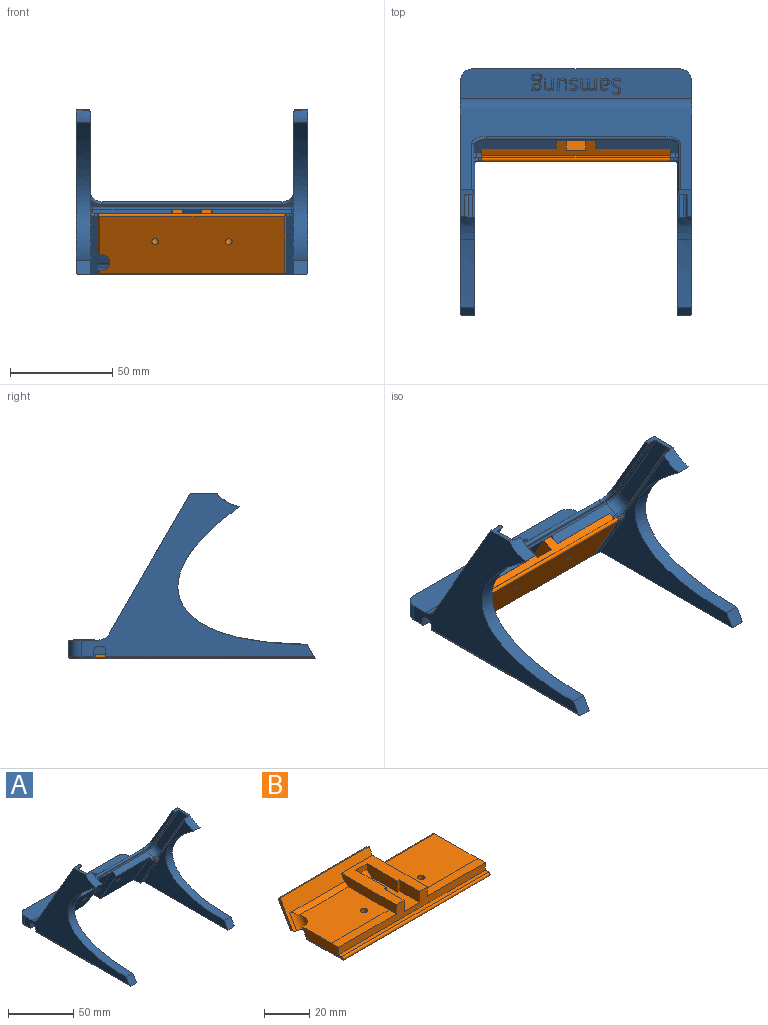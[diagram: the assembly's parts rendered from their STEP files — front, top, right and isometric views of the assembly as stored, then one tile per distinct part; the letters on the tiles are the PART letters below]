
ASSEMBLY  parts=2 mates=1
PART A: 272 faces, bbox 114x121.1x81.7 mm
  f0: plane 113x14.54mm, normal (0,0,1), area 1519mm2, adj f3,f5,f23,f48,f49,f50,f79,f80
  f1: plane 38.5x6.06mm, normal (0,-0.5,0.87), area 197.5mm2, adj f12,f28,f29,f47,f53,f64
  f2: plane 36x23.43mm, normal (0,-0.87,-0.5), area 952.4mm2, adj f13,f14,f19,f38,f41,f45
  f3: plane 113.96x79.65mm, normal (1,0,0), area 2704mm2, adj f0,f17,f18,f20,f31,f32,f48,f50
  f4: plane 50.89x29.38mm, normal (0,0.87,0.5), area 116mm2, adj f30,f54,f55,f56,f67,f68
  f5: plane 113.96x79.65mm, normal (-1,0,0), area 2676.7mm2, adj f0,f13,f20,f21,f22,f24,f25,f30
  f6: plane 47.03x33.21mm, normal (-1,0,0), area 366mm2, adj f32,f47,f51,f62
  f7: plane 47.03x33.21mm, normal (1,0,0), area 366mm2, adj f33,f46,f54,f66
  f8: plane 50.89x29.38mm, normal (0,0.87,0.5), area 116mm2, adj f31,f51,f52,f53,f70,f71
  f9: plane 91.57x79.61mm, normal (-1,0,0), area 1487.5mm2, adj f15,f17,f18,f27,f31,f70,f71
  f10: plane 91.57x79.61mm, normal (1,0,0), area 1487.5mm2, adj f11,f16,f21,f22,f30,f67,f68
  f11: plane 28.82x16.64mm, normal (0,-0.87,-0.5), area 114.3mm2, adj f10,f16,f19,f67,f69
  f12: plane 31.93x26.82mm, normal (-1,0,0), area 210.9mm2, adj f1,f13,f15,f25,f29,f40,f42,f43
  f13: plane 66.5x10.8mm, normal (0,0,-1), area 427.6mm2, adj f2,f5,f12,f19,f42,f43,f44,f45
  f14: plane 38.5x6.06mm, normal (0,-0.5,0.87), area 197.5mm2, adj f2,f19,f41,f46,f56,f64
  f15: plane 119.54x111mm, normal (0,0,-1), area 2295.9mm2, adj f9,f12,f18,f25,f27,f28,f29,f73
  f16: plane 102.33x9.5mm, normal (0,0,-1), area 651.6mm2, adj f10,f11,f19,f22,f24,f78
  f17: extruded ~67.37x63.17mm, area 886.2mm2, adj f3,f9,f18,f31
  f18: plane 7x6.93mm, normal (0,-0.87,0.5), area 55.8mm2, adj f3,f9,f15,f17,f73
  f19: plane 29.66x29.65mm, normal (1,0,0), area 234.7mm2, adj f2,f11,f13,f14,f16,f24,f44,f56
  f20: plane 113x68.65mm, normal (0,0.87,0.5), area 3620.6mm2, adj f3,f5,f32,f33,f50,f57,f58,f59
  f21: extruded ~67.37x63.17mm, area 886.2mm2, adj f5,f10,f22,f30
  f22: plane 7x6.93mm, normal (0,-0.87,0.5), area 55.8mm2, adj f5,f10,f16,f21,f78
  f23: plane 101x8mm, normal (0,1,0), area 808mm2, adj f0,f48,f49,f75
  f24: plane 10.5x3.5mm, normal (0,1,0), area 36.5mm2, adj f5,f16,f19,f44,f78
  f25: plane 66.5x3.5mm, normal (0,-1,0), area 232.5mm2, adj f5,f12,f15,f43,f77
  f26: plane 107x47.36mm, normal (0,-0.87,-0.5), area 385.7mm2, adj f32,f33,f57,f58,f59,f60,f61,f62
  f27: plane 28.82x16.64mm, normal (0,-0.87,-0.5), area 114.3mm2, adj f9,f15,f28,f71,f72
  f28: plane 29.66x23.32mm, normal (-1,0,0), area 199.9mm2, adj f1,f15,f27,f29,f53,f72
  f29: plane 36x29.43mm, normal (0,-0.87,-0.5), area 1210.7mm2, adj f1,f12,f15,f28,f35
  f30: extruded ~11x7mm, area 87.7mm2, adj f4,f5,f10,f21,f33,f54,f68
  f31: extruded ~11x7mm, area 87.7mm2, adj f3,f8,f9,f17,f32,f51,f70
  f32: plane 13.1x6.55mm, normal (0,0,1), area 36.5mm2, adj f3,f6,f20,f26,f31,f51,f57,f62
  f33: plane 13.1x6.55mm, normal (0,0,1), area 36.5mm2, adj f5,f7,f20,f26,f30,f54,f61,f66
  f34: cylinder r=1.5mm len=6.26mm, axis (0,-0.87,-0.5), area 51.8mm2, adj f35,f36
  f35: cone r=1.5mm half-angle=45deg, axis (0,-0.87,-0.5), area 7.8mm2, adj f29,f34
  f36: cone r=0mm half-angle=59deg, axis (0,-0.87,-0.5), area 8.2mm2, adj f34
  f37: cylinder r=1.5mm len=6.26mm, axis (0,-0.87,-0.5), area 51.8mm2, adj f38,f39
  f38: cone r=1.5mm half-angle=45deg, axis (0,-0.87,-0.5), area 7.8mm2, adj f2,f37
  f39: cone r=0mm half-angle=59deg, axis (0,-0.87,-0.5), area 8.2mm2, adj f37
  f40: plane 24.68x22.33mm, normal (0,-0.87,-0.5), area 573.8mm2, adj f12,f41,f42,f45,f64
  f41: plane 19.93x15.84mm, normal (1,0,0), area 107.8mm2, adj f2,f14,f40,f45
  f42: cylinder r=2.5mm len=26mm, axis (-1,0,0), area 63.3mm2, adj f12,f13,f40,f45
  f43: cylinder r=2.5mm len=66.5mm, axis (1,0,0), area 261.1mm2, adj f5,f12,f13,f25
  f44: cylinder r=2.5mm len=10.5mm, axis (-1,0,0), area 41.2mm2, adj f5,f13,f19,f24
  f45: cylinder r=6mm len=10.68mm, axis (0,-1,0), area 56.4mm2, adj f2,f13,f40,f41,f42
  f46: cylinder r=6mm len=9.06mm, axis (0,-0.87,-0.5), area 66mm2, adj f7,f14,f55,f65
  f47: cylinder r=6mm len=9.06mm, axis (0,0.87,0.5), area 66mm2, adj f1,f6,f52,f63
  f48: cylinder r=6mm len=8mm, axis (0,0,-1), area 75.4mm2, adj f0,f3,f23,f74
  f49: cylinder r=6mm len=8mm, axis (0,0,1), area 75.4mm2, adj f0,f5,f23,f76
  f50: cylinder r=6mm len=113mm, axis (-1,0,0), area 710mm2, adj f0,f3,f5,f20
  f51: cylinder r=2mm len=48.67mm, axis (0,0.5,-0.87), area 172.2mm2, adj f6,f8,f31,f32,f52
  f52: torus R=4mm, axis (0,-0.87,-0.5), area 26mm2, adj f8,f47,f51,f53
  f53: cylinder r=2mm len=2.73mm, axis (1,0,0), area 7.9mm2, adj f1,f8,f28,f52,f72
  f54: cylinder r=2mm len=48.67mm, axis (0,0.5,-0.87), area 172.2mm2, adj f4,f7,f30,f33,f55
  f55: torus R=4mm, axis (0,-0.87,-0.5), area 26mm2, adj f4,f46,f54,f56
  f56: cylinder r=2mm len=2.73mm, axis (1,0,0), area 7.9mm2, adj f4,f14,f19,f55,f69
  f57: cylinder r=1mm len=41.43mm, axis (0,-0.5,0.87), area 144.8mm2, adj f20,f26,f32,f58
  f58: torus R=7mm, axis (0,-0.87,-0.5), area 31.4mm2, adj f20,f26,f57,f59
  f59: cylinder r=1mm len=88mm, axis (1,0,0), area 276.5mm2, adj f20,f26,f58,f60
  f60: torus R=7mm, axis (0,-0.87,-0.5), area 31.4mm2, adj f20,f26,f59,f61
  f61: cylinder r=1mm len=41.43mm, axis (0,0.5,-0.87), area 144.8mm2, adj f20,f26,f33,f60
  f62: cylinder r=1mm len=44.03mm, axis (0,0.5,-0.87), area 78.4mm2, adj f6,f26,f32,f63
  f63: torus R=5mm, axis (0,0.87,0.5), area 13.9mm2, adj f26,f47,f62,f64
  f64: cylinder r=1mm len=97mm, axis (-1,0,0), area 152.4mm2, adj f1,f14,f26,f40,f63,f65
  f65: torus R=5mm, axis (0,0.87,0.5), area 13.9mm2, adj f26,f46,f64,f66
  f66: cylinder r=1mm len=44.03mm, axis (0,0.5,-0.87), area 78.4mm2, adj f7,f26,f33,f65
  f67: torus R=3mm, axis (0,-0.87,-0.5), area 9.8mm2, adj f4,f10,f11,f68,f69
  f68: cylinder r=1mm len=48.79mm, axis (0,-0.5,0.87), area 87.3mm2, adj f4,f10,f30,f67
  f69: cylinder r=1mm len=1.87mm, axis (1,0,0), area 4.7mm2, adj f11,f19,f56,f67
  f70: cylinder r=1mm len=48.79mm, axis (0,0.5,-0.87), area 87.3mm2, adj f8,f9,f31,f71
  f71: torus R=3mm, axis (0,-0.87,-0.5), area 9.8mm2, adj f8,f9,f27,f70,f72
  f72: cylinder r=1mm len=1.87mm, axis (1,0,0), area 4.7mm2, adj f27,f28,f53,f71
  f73: cylinder r=1mm len=114.54mm, axis (0,-1,0), area 179.6mm2, adj f3,f15,f18,f74
  f74: torus R=5mm, axis (0,0,-1), area 13.9mm2, adj f15,f48,f73,f75
  f75: cylinder r=1mm len=101mm, axis (1,0,0), area 158.7mm2, adj f15,f23,f74,f76
  f76: torus R=5mm, axis (0,0,-1), area 13.9mm2, adj f15,f49,f75,f77
  f77: cylinder r=1mm len=6.21mm, axis (0,1,0), area 9.7mm2, adj f5,f15,f25,f76
  f78: cylinder r=1mm len=102.33mm, axis (0,1,0), area 160.4mm2, adj f5,f16,f22,f24
  f79: extruded ~1.53x0.71mm, area 0.9mm2, adj f0,f80,f103,f104
  f80: extruded ~1.24x0.5mm, area 0.7mm2, adj f0,f79,f81,f104
  f81: extruded ~1.61x0.89mm, area 0.9mm2, adj f0,f80,f82,f104
  f82: extruded ~1.03x0.5mm, area 0.6mm2, adj f0,f81,f83,f104
  f83: extruded ~0.5x0.48mm, area 0.3mm2, adj f0,f82,f84,f104
  f84: extruded ~0.63x0.5mm, area 0.3mm2, adj f0,f83,f85,f104
  f85: extruded ~0.82x0.5mm, area 0.5mm2, adj f0,f84,f86,f104
  f86: extruded ~1.07x0.5mm, area 0.6mm2, adj f0,f85,f87,f104
  f87: extruded ~1.79x0.5mm, area 0.9mm2, adj f0,f86,f88,f104
  f88: plane 0.75x0.5mm, normal (-0.94,0.34,0), area 0.4mm2, adj f0,f87,f89,f104
  f89: extruded ~2.04x0.5mm, area 1mm2, adj f0,f88,f90,f104
  f90: extruded ~1.71x0.51mm, area 0.9mm2, adj f0,f89,f91,f104
  f91: extruded ~1.37x0.64mm, area 0.8mm2, adj f0,f90,f92,f104
  f92: extruded ~1.33x0.5mm, area 0.7mm2, adj f0,f91,f93,f104
  f93: extruded ~1.48x0.88mm, area 0.9mm2, adj f0,f92,f94,f104
  f94: extruded ~1.1x0.5mm, area 0.6mm2, adj f0,f93,f95,f104
  f95: extruded ~0.52x0.5mm, area 0.3mm2, adj f0,f94,f96,f104
  f96: extruded ~0.63x0.5mm, area 0.3mm2, adj f0,f95,f97,f104
  f97: extruded ~0.91x0.5mm, area 0.5mm2, adj f0,f96,f98,f104
  f98: extruded ~1.3x0.5mm, area 0.7mm2, adj f0,f97,f99,f104
  f99: extruded ~1.07x0.5mm, area 0.5mm2, adj f0,f98,f100,f104
  f100: extruded ~1x0.5mm, area 0.5mm2, adj f0,f99,f101,f104
  f101: plane 0.83x0.5mm, normal (1,0,0), area 0.4mm2, adj f0,f100,f102,f104
  f102: extruded ~2.03x0.5mm, area 1mm2, adj f0,f101,f103,f104
  f103: extruded ~1.93x0.55mm, area 1mm2, adj f0,f79,f102,f104
  f104: plane 7.64x4.67mm, normal (0,0,1), area 12.8mm2, adj f79,f80,f81,f82,f83,f84,f85,f86
  f105: extruded ~1.24x0.5mm, area 0.7mm2, adj f106,f131,f132,f133
  f106: extruded ~0.77x0.5mm, area 0.4mm2, adj f105,f107,f132,f133
  f107: extruded ~0.7x0.5mm, area 0.4mm2, adj f106,f108,f132,f133
  f108: extruded ~0.86x0.5mm, area 0.5mm2, adj f107,f109,f132,f133
  f109: extruded ~1.45x0.5mm, area 0.7mm2, adj f108,f110,f132,f133
  f110: plane 0.84x0.5mm, normal (-0.04,1,0), area 0.4mm2, adj f109,f111,f132,f133
  f111: plane 0.5x0.5mm, normal (1,0,0), area 0.3mm2, adj f110,f131,f132,f133
  f112: plane 0.79x0.5mm, normal (0.98,0.21,0), area 0.4mm2, adj f0,f113,f130,f132
  f113: plane 0.63x0.5mm, normal (0,1,0), area 0.3mm2, adj f0,f112,f114,f132
  f114: plane 3.8x0.5mm, normal (-1,0,0), area 1.9mm2, adj f0,f113,f115,f132
  f115: extruded ~1.42x0.5mm, area 0.8mm2, adj f0,f114,f116,f132
  f116: extruded ~1.48x0.5mm, area 0.8mm2, adj f0,f115,f117,f132
  f117: extruded ~0.98x0.5mm, area 0.5mm2, adj f0,f116,f118,f132
  f118: extruded ~0.9x0.5mm, area 0.5mm2, adj f0,f117,f119,f132
  f119: plane 0.65x0.5mm, normal (0.93,0.37,0), area 0.3mm2, adj f0,f118,f120,f132
  f120: extruded ~1.57x0.5mm, area 0.8mm2, adj f0,f119,f121,f132
  f121: extruded ~0.9x0.5mm, area 0.5mm2, adj f0,f120,f122,f132
  f122: extruded ~0.97x0.5mm, area 0.5mm2, adj f0,f121,f123,f132
  f123: plane 0.5x0.35mm, normal (1,0,0), area 0.2mm2, adj f0,f122,f124,f132
  f124: plane 0.94x0.5mm, normal (0.03,-1,0), area 0.5mm2, adj f0,f123,f125,f132
  f125: extruded ~2.7x1.77mm, area 1.8mm2, adj f0,f124,f126,f132
  f126: extruded ~1.21x0.5mm, area 0.7mm2, adj f0,f125,f127,f132
  f127: extruded ~1.3x0.5mm, area 0.7mm2, adj f0,f126,f128,f132
  f128: extruded ~1.03x0.5mm, area 0.5mm2, adj f0,f127,f129,f132
  f129: extruded ~0.83x0.71mm, area 0.6mm2, adj f0,f128,f130,f132
  f130: plane 0.5x0.04mm, normal (0,1,0), area 0mm2, adj f0,f112,f129,f132
  f131: extruded ~1.21x0.5mm, area 0.7mm2, adj f105,f111,f132,f133
  f132: plane 5.76x4.47mm, normal (0,0,1), area 12.1mm2, adj f105,f106,f107,f108,f109,f110,f111,f112
  f133: plane 2.74x2.14mm, normal (0,0,1), area 4.7mm2, adj f105,f106,f107,f108,f109,f110,f111,f131
  f134: plane 3.62x0.5mm, normal (1,0,0), area 1.8mm2, adj f0,f135,f161,f162
  f135: plane 0.84x0.5mm, normal (0,1,0), area 0.4mm2, adj f0,f134,f136,f162
  f136: plane 3.63x0.5mm, normal (-1,0,0), area 1.8mm2, adj f0,f135,f137,f162
  f137: extruded ~1.55x0.5mm, area 0.8mm2, adj f0,f136,f138,f162
  f138: extruded ~1.41x0.5mm, area 0.8mm2, adj f0,f137,f139,f162
  f139: extruded ~1.08x0.5mm, area 0.6mm2, adj f0,f138,f140,f162
  f140: extruded ~0.72x0.69mm, area 0.5mm2, adj f0,f139,f141,f162
  f141: plane 0.5x0.04mm, normal (0,-1,0), area 0mm2, adj f0,f140,f142,f162
  f142: extruded ~1.71x0.95mm, area 1mm2, adj f0,f141,f143,f162
  f143: extruded ~0.97x0.5mm, area 0.5mm2, adj f0,f142,f144,f162
  f144: extruded ~0.67x0.64mm, area 0.5mm2, adj f0,f143,f145,f162
  f145: plane 0.5x0.04mm, normal (0,-1,0), area 0mm2, adj f0,f144,f146,f162
  f146: plane 0.76x0.5mm, normal (-0.98,-0.18,0), area 0.4mm2, adj f0,f145,f147,f162
  f147: plane 0.69x0.5mm, normal (0,-1,0), area 0.3mm2, adj f0,f146,f148,f162
  f148: plane 5.57x0.5mm, normal (1,0,0), area 2.8mm2, adj f0,f147,f149,f162
  f149: plane 0.84x0.5mm, normal (0,1,0), area 0.4mm2, adj f0,f148,f150,f162
  f150: plane 2.92x0.5mm, normal (-1,0,0), area 1.5mm2, adj f0,f149,f151,f162
  f151: extruded ~1.56x0.5mm, area 0.8mm2, adj f0,f150,f152,f162
  f152: extruded ~1.16x0.5mm, area 0.7mm2, adj f0,f151,f153,f162
  f153: extruded ~0.89x0.5mm, area 0.5mm2, adj f0,f152,f154,f162
  f154: extruded ~1x0.5mm, area 0.5mm2, adj f0,f153,f155,f162
  f155: plane 3.62x0.5mm, normal (1,0,0), area 1.8mm2, adj f0,f154,f156,f162
  f156: plane 0.84x0.5mm, normal (0,1,0), area 0.4mm2, adj f0,f155,f157,f162
  f157: plane 3.11x0.5mm, normal (-1,0,0), area 1.6mm2, adj f0,f156,f158,f162
  f158: extruded ~1.39x0.5mm, area 0.7mm2, adj f0,f157,f159,f162
  f159: extruded ~1.16x0.5mm, area 0.6mm2, adj f0,f158,f160,f162
  f160: extruded ~0.88x0.5mm, area 0.5mm2, adj f0,f159,f161,f162
  f161: extruded ~1x0.5mm, area 0.5mm2, adj f0,f134,f160,f162
  f162: plane 7.94x5.67mm, normal (0,0,1), area 17.6mm2, adj f134,f135,f136,f137,f138,f139,f140,f141
  f163: extruded ~1.2x0.58mm, area 0.7mm2, adj f0,f164,f187,f188
  f164: extruded ~0.92x0.5mm, area 0.5mm2, adj f0,f163,f165,f188
  f165: extruded ~1.34x0.73mm, area 0.8mm2, adj f0,f164,f166,f188
  f166: extruded ~0.98x0.5mm, area 0.5mm2, adj f0,f165,f167,f188
  f167: extruded ~0.5x0.37mm, area 0.2mm2, adj f0,f166,f168,f188
  f168: extruded ~0.5x0.38mm, area 0.2mm2, adj f0,f167,f169,f188
  f169: extruded ~0.52x0.5mm, area 0.3mm2, adj f0,f168,f170,f188
  f170: extruded ~0.9x0.5mm, area 0.5mm2, adj f0,f169,f171,f188
  f171: extruded ~1.52x0.5mm, area 0.8mm2, adj f0,f170,f172,f188
  f172: plane 0.69x0.5mm, normal (-0.92,0.4,0), area 0.4mm2, adj f0,f171,f173,f188
  f173: extruded ~1.76x0.5mm, area 0.9mm2, adj f0,f172,f174,f188
  f174: extruded ~1.52x0.5mm, area 0.8mm2, adj f0,f173,f175,f188
  f175: extruded ~1.08x0.55mm, area 0.6mm2, adj f0,f174,f176,f188
  f176: extruded ~0.65x0.5mm, area 0.3mm2, adj f0,f175,f177,f188
  f177: extruded ~0.5x0.49mm, area 0.3mm2, adj f0,f176,f178,f188
  f178: extruded ~1.1x0.51mm, area 0.6mm2, adj f0,f177,f179,f188
  f179: extruded ~1.1x0.55mm, area 0.6mm2, adj f0,f178,f180,f188
  f180: extruded ~0.56x0.5mm, area 0.3mm2, adj f0,f179,f181,f188
  f181: extruded ~0.64x0.5mm, area 0.4mm2, adj f0,f180,f182,f188
  f182: extruded ~1.02x0.5mm, area 0.5mm2, adj f0,f181,f183,f188
  f183: extruded ~0.89x0.5mm, area 0.4mm2, adj f0,f182,f184,f188
  f184: extruded ~0.86x0.5mm, area 0.5mm2, adj f0,f183,f185,f188
  f185: plane 0.78x0.5mm, normal (1,0,0), area 0.4mm2, adj f0,f184,f186,f188
  f186: extruded ~1.73x0.5mm, area 0.9mm2, adj f0,f185,f187,f188
  f187: extruded ~1.63x0.5mm, area 0.9mm2, adj f0,f163,f186,f188
  f188: plane 5.77x3.95mm, normal (0,0,1), area 9.5mm2, adj f163,f164,f165,f166,f167,f168,f169,f170
  f189: plane 3.61x0.5mm, normal (-1,0,0), area 1.8mm2, adj f0,f190,f205,f206
  f190: plane 0.85x0.5mm, normal (0,-1,0), area 0.4mm2, adj f0,f189,f191,f206
  f191: plane 3.64x0.5mm, normal (1,0,0), area 1.8mm2, adj f0,f190,f192,f206
  f192: extruded ~1.54x0.5mm, area 0.8mm2, adj f0,f191,f193,f206
  f193: extruded ~1.52x0.5mm, area 0.8mm2, adj f0,f192,f194,f206
  f194: extruded ~1.05x0.5mm, area 0.5mm2, adj f0,f193,f195,f206
  f195: extruded ~0.72x0.63mm, area 0.5mm2, adj f0,f194,f196,f206
  f196: plane 0.5x0.05mm, normal (0,1,0), area 0mm2, adj f0,f195,f197,f206
  f197: plane 0.75x0.5mm, normal (0.99,0.16,0), area 0.4mm2, adj f0,f196,f198,f206
  f198: plane 0.7x0.5mm, normal (0,1,0), area 0.3mm2, adj f0,f197,f199,f206
  f199: plane 5.57x0.5mm, normal (-1,0,0), area 2.8mm2, adj f0,f198,f200,f206
  f200: plane 0.84x0.5mm, normal (0,-1,0), area 0.4mm2, adj f0,f199,f201,f206
  f201: plane 2.93x0.5mm, normal (1,0,0), area 1.5mm2, adj f0,f200,f202,f206
  f202: extruded ~1.56x0.5mm, area 0.8mm2, adj f0,f201,f203,f206
  f203: extruded ~1.28x0.5mm, area 0.7mm2, adj f0,f202,f204,f206
  f204: extruded ~0.97x0.5mm, area 0.5mm2, adj f0,f203,f205,f206
  f205: extruded ~1.02x0.5mm, area 0.5mm2, adj f0,f189,f204,f206
  f206: plane 5.67x4.66mm, normal (0,0,1), area 11.3mm2, adj f189,f190,f191,f192,f193,f194,f195,f196
  f207: plane 3.6x0.5mm, normal (1,0,0), area 1.8mm2, adj f0,f208,f223,f224
  f208: plane 0.84x0.5mm, normal (0,1,0), area 0.4mm2, adj f0,f207,f209,f224
  f209: plane 3.63x0.5mm, normal (-1,0,0), area 1.8mm2, adj f0,f208,f210,f224
  f210: extruded ~1.55x0.51mm, area 0.8mm2, adj f0,f209,f211,f224
  f211: extruded ~1.51x0.5mm, area 0.8mm2, adj f0,f210,f212,f224
  f212: extruded ~1.04x0.5mm, area 0.5mm2, adj f0,f211,f213,f224
  f213: extruded ~0.73x0.64mm, area 0.5mm2, adj f0,f212,f214,f224
  f214: plane 0.5x0.04mm, normal (0,-1,0), area 0mm2, adj f0,f213,f215,f224
  f215: plane 0.76x0.5mm, normal (-0.98,-0.18,0), area 0.4mm2, adj f0,f214,f216,f224
  f216: plane 0.69x0.5mm, normal (0,-1,0), area 0.3mm2, adj f0,f215,f217,f224
  f217: plane 5.57x0.5mm, normal (1,0,0), area 2.8mm2, adj f0,f216,f218,f224
  f218: plane 0.84x0.5mm, normal (0,1,0), area 0.4mm2, adj f0,f217,f219,f224
  f219: plane 2.92x0.5mm, normal (-1,0,0), area 1.5mm2, adj f0,f218,f220,f224
  f220: extruded ~1.56x0.5mm, area 0.8mm2, adj f0,f219,f221,f224
  f221: extruded ~1.28x0.5mm, area 0.7mm2, adj f0,f220,f222,f224
  f222: extruded ~0.97x0.5mm, area 0.5mm2, adj f0,f221,f223,f224
  f223: extruded ~1.02x0.5mm, area 0.5mm2, adj f0,f207,f222,f224
  f224: plane 5.67x4.65mm, normal (0,0,1), area 11.2mm2, adj f207,f208,f209,f210,f211,f212,f213,f214
  f225: extruded ~0.88x0.5mm, area 0.5mm2, adj f226,f268,f269,f270
  f226: extruded ~0.95x0.5mm, area 0.5mm2, adj f225,f227,f269,f270
  f227: extruded ~0.92x0.5mm, area 0.5mm2, adj f226,f228,f269,f270
  f228: extruded ~1.25x1.25mm, area 1mm2, adj f227,f229,f269,f270
  f229: extruded ~1.23x1.2mm, area 1mm2, adj f228,f268,f269,f270
  f230: extruded ~0.69x0.5mm, area 0.4mm2, adj f231,f266,f269,f271
  f231: extruded ~0.79x0.5mm, area 0.4mm2, adj f230,f232,f269,f271
  f232: extruded ~0.89x0.5mm, area 0.5mm2, adj f231,f233,f269,f271
  f233: plane 1.01x0.5mm, normal (0,1,0), area 0.5mm2, adj f232,f234,f269,f271
  f234: extruded ~1.05x0.5mm, area 0.5mm2, adj f233,f235,f269,f271
  f235: extruded ~0.63x0.5mm, area 0.4mm2, adj f234,f236,f269,f271
  f236: extruded ~0.86x0.51mm, area 0.5mm2, adj f235,f237,f269,f271
  f237: extruded ~1.57x0.5mm, area 0.8mm2, adj f236,f266,f269,f271
  f238: plane 0.53x0.5mm, normal (-1,0,0), area 0.3mm2, adj f0,f239,f267,f269
  f239: plane 1.92x0.5mm, normal (0,-1,0), area 1mm2, adj f0,f238,f240,f269
  f240: extruded ~0.79x0.5mm, area 0.4mm2, adj f0,f239,f241,f269
  f241: extruded ~1.55x0.5mm, area 0.8mm2, adj f0,f240,f242,f269
  f242: extruded ~1.41x0.55mm, area 0.8mm2, adj f0,f241,f243,f269
  f243: extruded ~0.98x0.5mm, area 0.5mm2, adj f0,f242,f244,f269
  f244: extruded ~0.7x0.6mm, area 0.5mm2, adj f0,f243,f245,f269
  f245: extruded ~0.51x0.5mm, area 0.3mm2, adj f0,f244,f246,f269
  f246: extruded ~0.53x0.5mm, area 0.3mm2, adj f0,f245,f247,f269
  f247: extruded ~0.5x0.47mm, area 0.3mm2, adj f0,f246,f248,f269
  f248: extruded ~0.5x0.36mm, area 0.2mm2, adj f0,f247,f249,f269
  f249: extruded ~0.91x0.5mm, area 0.5mm2, adj f0,f248,f250,f269
  f250: extruded ~0.88x0.5mm, area 0.5mm2, adj f0,f249,f251,f269
  f251: extruded ~1.15x0.59mm, area 0.7mm2, adj f0,f250,f252,f269
  f252: extruded ~1.68x0.5mm, area 0.9mm2, adj f0,f251,f253,f269
  f253: extruded ~2.16x0.5mm, area 1.1mm2, adj f0,f252,f254,f269
  f254: extruded ~1.41x0.74mm, area 0.8mm2, adj f0,f253,f255,f269
  f255: extruded ~1.11x0.5mm, area 0.6mm2, adj f0,f254,f256,f269
  f256: extruded ~1.39x0.5mm, area 0.7mm2, adj f0,f255,f257,f269
  f257: plane 0.99x0.5mm, normal (0,-1,0), area 0.5mm2, adj f0,f256,f258,f269
  f258: extruded ~0.64x0.5mm, area 0.3mm2, adj f0,f257,f259,f269
  f259: extruded ~0.5x0.34mm, area 0.2mm2, adj f0,f258,f260,f269
  f260: extruded ~0.72x0.54mm, area 0.5mm2, adj f0,f259,f261,f269
  f261: extruded ~0.5x0.47mm, area 0.2mm2, adj f0,f260,f262,f269
  f262: extruded ~1.53x0.5mm, area 0.8mm2, adj f0,f261,f263,f269
  f263: extruded ~1.31x0.56mm, area 0.7mm2, adj f0,f262,f264,f269
  f264: extruded ~0.65x0.5mm, area 0.3mm2, adj f0,f263,f265,f269
  f265: extruded ~0.5x0.47mm, area 0.3mm2, adj f0,f264,f267,f269
  f266: extruded ~1.09x0.5mm, area 0.6mm2, adj f230,f237,f269,f271
  f267: plane 1.03x0.5mm, normal (-0.12,0.99,0), area 0.5mm2, adj f0,f238,f265,f269
  f268: extruded ~0.92x0.5mm, area 0.5mm2, adj f225,f229,f269,f270
  f269: plane 8.17x5.25mm, normal (0,0,1), area 17.8mm2, adj f225,f226,f227,f228,f229,f230,f231,f232
  f270: plane 2.48x2.45mm, normal (0,0,1), area 5.1mm2, adj f225,f226,f227,f228,f229,f268
  f271: plane 3.56x1.98mm, normal (0,0,1), area 6mm2, adj f230,f231,f232,f233,f234,f235,f236,f237
PART B: 37 faces, bbox 92x40.9x18.4 mm
  f0: plane 92x9mm, normal (0,-1,0), area 411.3mm2, adj f1,f4,f7,f11,f16,f17,f18,f20
  f1: plane 25.82x5.05mm, normal (-1,0,0), area 109.9mm2, adj f0,f5,f6,f7,f20,f22,f24,f26
  f2: plane 55.75x1.3mm, normal (0,0.5,0.87), area 83.6mm2, adj f3,f8,f13,f16
  f3: plane 92x13.91mm, normal (0,0.87,-0.5), area 1114.7mm2, adj f2,f4,f12,f13,f16,f19,f23,f25
  f4: plane 35.85x5.05mm, normal (1,0,0), area 161.6mm2, adj f0,f3,f9,f10,f11,f19,f20,f24
  f5: plane 36.25x25.32mm, normal (0,0,1), area 873.3mm2, adj f1,f6,f15,f17,f21,f22,f35
  f6: plane 36.25x0.05mm, normal (0,1,0), area 2mm2, adj f1,f5,f7,f17
  f7: plane 36.25x4.5mm, normal (0,0,1), area 163.1mm2, adj f0,f1,f6,f17
  f8: plane 55.75x14.66mm, normal (0,-0.87,0.5), area 399.2mm2, adj f2,f12,f13,f16,f17,f18,f21,f23
  f9: plane 36.25x27.05mm, normal (0,0,1), area 972.3mm2, adj f4,f10,f14,f16,f19
  f10: plane 36.25x0.05mm, normal (0,1,0), area 2mm2, adj f4,f9,f11,f16
  f11: plane 36.25x4.5mm, normal (0,0,1), area 163.1mm2, adj f0,f4,f10,f16
  f12: plane 90x31.82mm, normal (0,0,-1), area 2812.5mm2, adj f3,f8,f14,f15,f21,f22,f23,f24
  f13: plane 13.66x9.19mm, normal (-1,0,0), area 23mm2, adj f2,f3,f8,f23
  f14: cylinder r=1.62mm len=6mm, axis (0,0,1), area 61.3mm2, adj f9,f12
  f15: cylinder r=1.62mm len=6mm, axis (0,0,1), area 61.3mm2, adj f5,f12
  f16: plane 37.85x9.41mm, normal (1,0,0), area 179.7mm2, adj f0,f2,f3,f8,f9,f10,f11,f18
  f17: plane 34.44x5mm, normal (-1,0,0), area 163.4mm2, adj f0,f5,f6,f7,f8,f18,f35
  f18: plane 34.44x19.5mm, normal (0,0,1), area 416.9mm2, adj f0,f8,f16,f17,f27,f28,f29,f30
  f19: plane 36.25x1.3mm, normal (0,0.5,0.87), area 54.4mm2, adj f3,f4,f9,f16
  f20: plane 92x2mm, normal (0,0,1), area 184mm2, adj f0,f1,f4,f24
  f21: cylinder r=3.78mm len=15.06mm, axis (0,0.5,0.87), area 86.2mm2, adj f5,f8,f12,f22,f35
  f22: plane 6x3.46mm, normal (0,0.87,-0.5), area 13.6mm2, adj f1,f5,f12,f21,f26
  f23: cylinder r=1mm len=2.31mm, axis (0,1,0), area 2.7mm2, adj f3,f8,f12,f13
  f24: cylinder r=1mm len=92mm, axis (1,0,0), area 287.9mm2, adj f1,f4,f12,f20,f25,f26
  f25: cylinder r=1mm len=33.4mm, axis (0,-1,0), area 51.3mm2, adj f3,f4,f12,f24
  f26: cylinder r=1mm len=22.94mm, axis (0,1,0), area 34.9mm2, adj f1,f12,f22,f24
  f27: plane 19.05x6mm, normal (1,0,0), area 109.8mm2, adj f18,f28,f33,f34,f36
  f28: plane 6x1.35mm, normal (0,-1,0), area 8.1mm2, adj f18,f27,f29,f34
  f29: plane 12.5x6mm, normal (1,0,0), area 75mm2, adj f0,f18,f28,f34
  f30: plane 12.5x6mm, normal (-1,0,0), area 75mm2, adj f0,f18,f31,f34
  f31: plane 6x1.35mm, normal (0,-1,0), area 8.1mm2, adj f18,f30,f32,f34
  f32: plane 19.05x6mm, normal (-1,0,0), area 109.8mm2, adj f18,f31,f33,f34,f36
  f33: plane 7x3mm, normal (0,-1,0), area 21mm2, adj f18,f27,f32,f36
  f34: plane 28.55x9.7mm, normal (0,0,1), area 233.6mm2, adj f0,f27,f28,f29,f30,f31,f32,f36
  f35: plane 34.25x2.6mm, normal (0,-0.5,0.87), area 96.4mm2, adj f5,f8,f17,f21
  f36: plane 7x3mm, normal (0,-0.71,0.71), area 29.7mm2, adj f27,f32,f33,f34
PLACE A t=(-50.5,-12,-9)mm
PLACE B rot(axis=(-1,0,0),60deg) t=(-50.5,40.21,-118.43)mm
MATE slider B.f14 <-> A.f36  axis (0,0.87,0.5) through (-32.5,-27.03,10.03)mm
